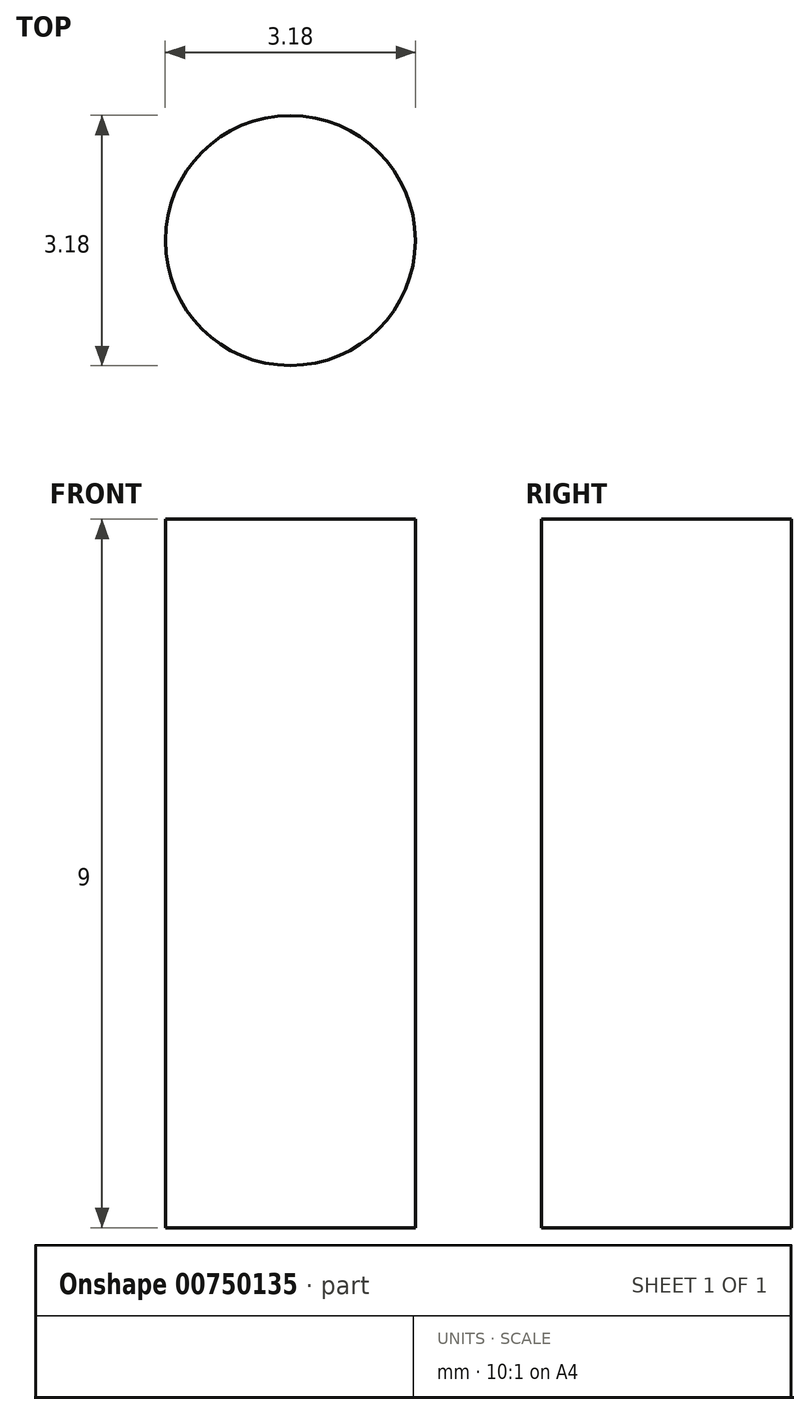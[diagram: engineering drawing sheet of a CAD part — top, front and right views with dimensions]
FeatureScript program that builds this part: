
annotation { "Feature Type Name" : "Feature", "Feature Type Description" : "" }
export const myFeature = defineFeature(function(context is Context, id is Id, definition is map)
    precondition{}
    {
        {
            assignVariable(context, id + "F0", {"name" : "wood", "anyValue" : 9});
        }
        {
            var Q0;
            Q0=qCreatedBy(makeId("Front.planeOp"),FACE);
            var sketch = newSketch(context, id + "F1", { "sketchPlane" : qUnion([Q0])});
            skLineSegment(sketch, "E0", {"start": v(1.59, 0) * mm, "end": v(1.59, -8) * mm});
            skLineSegment(sketch, "E1", {"start": v(1.59, -8) * mm, "end": v(8.25, -8) * mm});
            skLineSegment(sketch, "E2", {"start": v(8.25, -8) * mm, "end": v(8.25, -19.5) * mm});
            skLineSegment(sketch, "E3.MirrorCS", {"start": v(-8.25, -8) * mm, "end": v(-8.25, -19.5) * mm});
            skLineSegment(sketch, "E4.MirrorCS", {"start": v(-1.59, -8) * mm, "end": v(-8.25, -8) * mm});
            skLineSegment(sketch, "E5.MirrorCS", {"start": v(-1.59, 0) * mm, "end": v(-1.59, -8) * mm});
            skLineSegment(sketch, "E6", {"start": v(8.25, -19.5) * mm, "end": v(-8.25, -19.5) * mm});
            skLineSegment(sketch, "E7", {"start": v(-1.59, 0) * mm, "end": v(1.59, 0) * mm});
            skSolve(sketch);
        }
        {
            var Q0;
            Q0=makeQuery(id+"F1.imprint","IMPRINT",FACE,{"disambiguationData":[TD([[makeQuery(id+"F1.imprint","IMPRINT",EDGE,{"derivedFrom":sQuery(id+"F1.wireOp",EDGE,"E0")}),-1.0]])]});
            extrude(context, id + "F2", {"entities" : qUnion([Q0]), "depth" : (getVariable(context, 'wood') + 1) * mm, "offsetDistance" : 25 * mm, "symmetric" : true});
        }
        {
            var Q0;
            Q0=qCreatedBy(makeId("Top.planeOp"),FACE);
            var sketch = newSketch(context, id + "F3", { "sketchPlane" : qUnion([Q0])});
            skCircle(sketch, "E8", {"center": v(0, 0) * mm, "radius": 1.59 * mm});
            skSolve(sketch);
        }
        {
            var Q0;
            Q0=makeQuery(id+"F3.imprint","IMPRINT",FACE,{"disambiguationData":[TD([[makeQuery(id+"F3.imprint","IMPRINT",EDGE,{"derivedFrom":sQuery(id+"F3.wireOp",EDGE,"E8")}),1.0]])]});
            extrude(context, id + "F4", {"entities" : qUnion([Q0]), "operationType" : NewBodyOperationType.ADD, "depth" : (getVariable(context, 'wood')) * mm, "offsetDistance" : 25 * mm});
        }
        {
            var Q0;
            Q0=makeQuery(id+"F2.opExtrude","CAP_FACE",FACE,{"disambiguationData":[OSD([sQuery(id+"F1.wireOp",EDGE,"E0"),sQuery(id+"F1.wireOp",EDGE,"E1"),sQuery(id+"F1.wireOp",EDGE,"E2"),sQuery(id+"F1.wireOp",EDGE,"E3.MirrorCS"),sQuery(id+"F1.wireOp",EDGE,"E4.MirrorCS"),sQuery(id+"F1.wireOp",EDGE,"E5.MirrorCS"),sQuery(id+"F1.wireOp",EDGE,"E6"),sQuery(id+"F1.wireOp",EDGE,"E7")])],"isStart":false});
            extrude(context, id + "F5", {"entities" : qUnion([Q0]), "operationType" : NewBodyOperationType.REMOVE, "oppositeDirection" : true, "depth" : 25 * mm, "offsetDistance" : 25 * mm});
        }
    });
